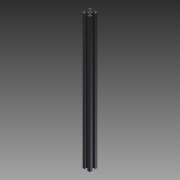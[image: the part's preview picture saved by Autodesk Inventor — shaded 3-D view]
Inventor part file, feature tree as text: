
AUTODESK INVENTOR PART (.ipt)
format: ipt  version: 2014 SP1 (Build 180222100, 222)  size: 177,152 bytes
history: native  units: mm
features: other x7, sketch x2, extrude x1, revolve x1
ambient origin geometry x8: Origin, YZ Plane, XZ Plane, XY Plane, X Axis, Y Axis, Z Axis, Center Point
bodies: Solid1 (feature_tree)
feature tree (11):
  extrude  "Extrusion1"  TaperAngle=360.0deg  [1 undecoded]
  revolve  "Revolution1"  [1 undecoded]
  other  "C1_XY"
  other  "C1_YZ"
  other  "C1_ZX"
  other  "C1_X"
  other  "C1_Y"
  other  "C1_Z"
  other  "C1_Center"
  sketch  "Sketch_1"  dims[d0=350.513mm d1=0.0mm d2=360.0deg]
  sketch  "Sketch_2"
note: 2 required parameter values undecoded (feature->parameter linkage not recoverable at this tier; creation-order binding heuristic only, values carry confidence <= 0.55)
